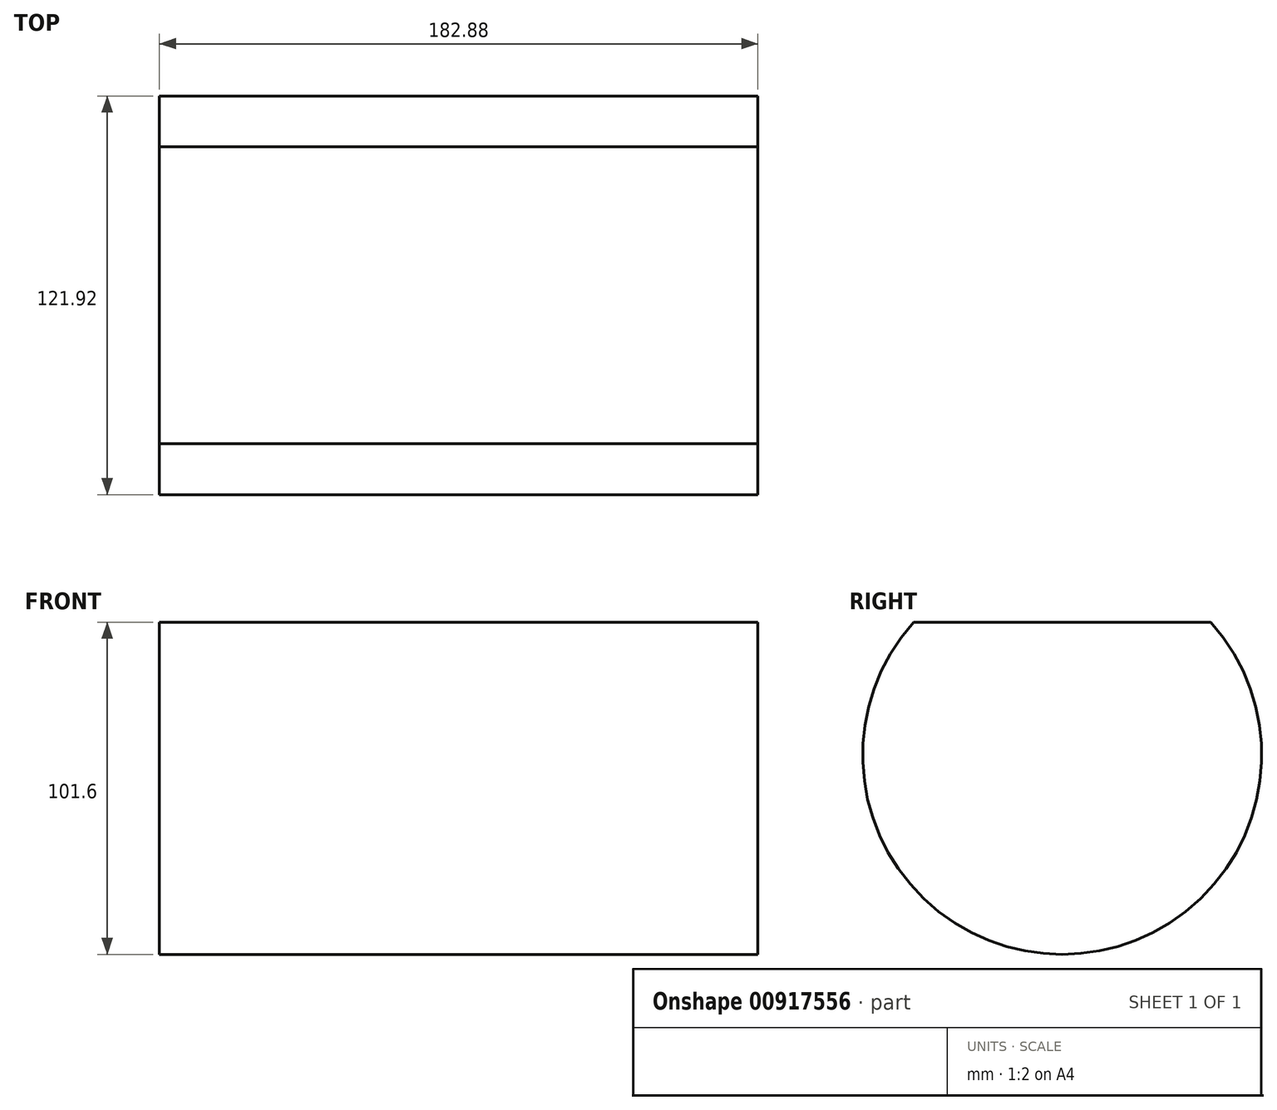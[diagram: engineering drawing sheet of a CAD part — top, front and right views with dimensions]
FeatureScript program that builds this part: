
annotation { "Feature Type Name" : "Feature", "Feature Type Description" : "" }
export const myFeature = defineFeature(function(context is Context, id is Id, definition is map)
    precondition{}
    {
        {
            var Q0;
            Q0=qCreatedBy(makeId("Right.planeOp"),FACE);
            var sketch = newSketch(context, id + "F0", { "sketchPlane" : qUnion([Q0])});
            skCircle(sketch, "E0", {"center": v(0, 0) * mm, "radius": 60.96 * mm});
            skLineSegment(sketch, "E1", {"start": v(-45.44, 40.64) * mm, "end": v(45.44, 40.64) * mm});
            skLineSegment(sketch, "E2", {"start": v(0, -60.96) * mm, "end": v(0, 40.64) * mm});
            skSolve(sketch);
        }
        {
            var Q0;
            {var subQ3=sQuery(id+"F0.wireOp",EDGE,"E2");Q0=makeQuery(id+"F0.imprint","IMPRINT",FACE,{"disambiguationData":[TD([[makeQuery(id+"F0.imprint","IMPRINT",EDGE,{"derivedFrom":subQ3}),1.0]])]});}
            var Q1;
            {var subQ3=sQuery(id+"F0.wireOp",EDGE,"E2");Q1=makeQuery(id+"F0.imprint","IMPRINT",FACE,{"disambiguationData":[TD([[makeQuery(id+"F0.imprint","IMPRINT",EDGE,{"derivedFrom":subQ3}),-1.0]])]});}
            extrude(context, id + "F1", {"entities" : qUnion([Q0, Q1]), "depth" : 182.88 * mm, "offsetDistance" : 25.4 * mm});
        }
    });
